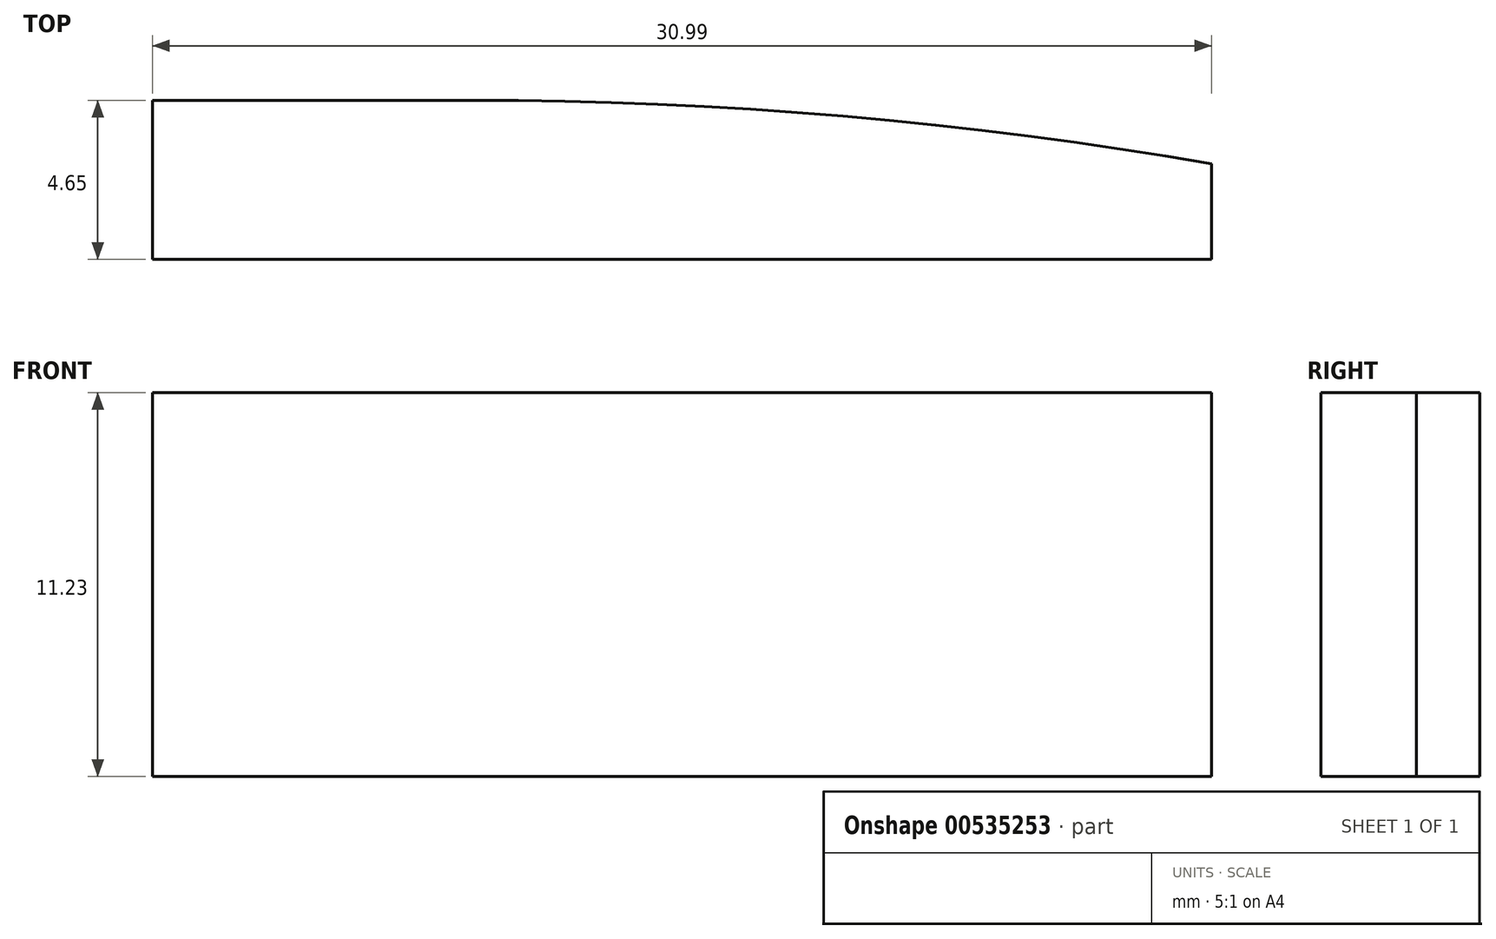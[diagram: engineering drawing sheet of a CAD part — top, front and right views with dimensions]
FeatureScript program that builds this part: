
annotation { "Feature Type Name" : "Feature", "Feature Type Description" : "" }
export const myFeature = defineFeature(function(context is Context, id is Id, definition is map)
    precondition{}
    {
        {
            var Q0;
            Q0=qCreatedBy(makeId("Front.planeOp"),FACE);
            var sketch = newSketch(context, id + "F0", { "sketchPlane" : qUnion([Q0])});
            skLineSegment(sketch, "E0.bottom", {"start": v(30.99, 11.23) * mm, "end": v(0, 11.23) * mm});
            skLineSegment(sketch, "E0.top", {"start": v(30.99, 0) * mm, "end": v(0, 0) * mm});
            skLineSegment(sketch, "E0.left", {"start": v(30.99, 11.23) * mm, "end": v(30.99, 0) * mm});
            skLineSegment(sketch, "E0.right", {"start": v(0, 11.23) * mm, "end": v(0, 0) * mm});
            skSolve(sketch);
        }
        {
            var Q0;
            Q0 = qSketchRegion(id + "F0", true);
            extrude(context, id + "F1", {"entities" : qUnion([Q0]), "depth" : 1.86 * mm, "offsetDistance" : 25.4 * mm});
        }
        {
            var Q0;
            Q0=makeQuery(id+"F1.opExtrude","CAP_FACE",FACE,{"disambiguationData":[OSD([sQuery(id+"F0.wireOp",EDGE,"E0.bottom"),sQuery(id+"F0.wireOp",EDGE,"E0.top"),sQuery(id+"F0.wireOp",EDGE,"E0.left"),sQuery(id+"F0.wireOp",EDGE,"E0.right")])],"isStart":false});
            var sketch = newSketch(context, id + "F2", { "sketchPlane" : qUnion([Q0])});
            skLineSegment(sketch, "E1.bottom", {"start": v(0, 0) * mm, "end": v(0, 0) * mm});
            skLineSegment(sketch, "E1.top", {"start": v(0, 11.23) * mm, "end": v(0, 11.23) * mm});
            skLineSegment(sketch, "E1.left", {"start": v(0, 0) * mm, "end": v(0, 11.23) * mm});
            skLineSegment(sketch, "E1.right", {"start": v(0, 0) * mm, "end": v(0, 11.23) * mm});
            skLineSegment(sketch, "E2.bottom", {"start": v(30.99, 11.23) * mm, "end": v(30.99, 11.23) * mm});
            skLineSegment(sketch, "E2.top", {"start": v(30.99, 0) * mm, "end": v(30.99, 0) * mm});
            skLineSegment(sketch, "E2.left", {"start": v(30.99, 11.23) * mm, "end": v(30.99, 0) * mm});
            skLineSegment(sketch, "E2.right", {"start": v(30.99, 11.23) * mm, "end": v(30.99, 0) * mm});
            skLineSegment(sketch, "E3.bottom", {"start": v(0, 11.23) * mm, "end": v(30.99, 11.23) * mm});
            skLineSegment(sketch, "E3.top", {"start": v(0, 11.23) * mm, "end": v(30.99, 11.23) * mm});
            skLineSegment(sketch, "E4.bottom", {"start": v(0, 0) * mm, "end": v(30.99, 0) * mm});
            skLineSegment(sketch, "E4.top", {"start": v(0, 0) * mm, "end": v(30.99, 0) * mm});
            skSolve(sketch);
        }
        {
            var Q0;
            Q0=makeQuery(id+"F1.opExtrude","CAP_EDGE",EDGE,{"disambiguationData":[OSD([sQuery(id+"F0.wireOp",EDGE,"E0.left")])],"isStart":true});
            fillet(context, id + "F3", {"entities" : qUnion([Q0]), "radius" : 127 * mm, "tangentPropagation" : true, "allowEdgeOverflow" : false});
        }
        {
            var Q0;
            Q0 = qSketchRegion(id + "F2", true);
            extrude(context, id + "F4", {"entities" : qUnion([Q0]), "operationType" : NewBodyOperationType.ADD, "depth" : 2.8 * mm, "offsetDistance" : 25.4 * mm});
        }
    });
